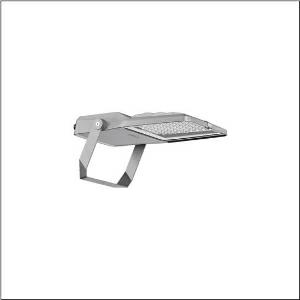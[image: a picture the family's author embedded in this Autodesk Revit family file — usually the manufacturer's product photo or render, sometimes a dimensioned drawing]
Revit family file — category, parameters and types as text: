
# Revit family: floodlight_fl_21_mini___pl33t_5xa7772b2f1a_c476
name_source: partatom
category: Lighting Fixtures
units: mm (PartAtom-declared; Revit-internal decimal feet)

## family parameters
Cut with Voids When Loaded = No
Host = Face
Light Source = No
Part Type = Normal
Room Calculation Point = No
Round Connector Dimension = Use Diameter
Shared = No

## types (1)
- --- (1 x LED, 6170 lm, 45.5 W, 3000K)
    Apparent Load = 46 VA
    CIE Flux Codes = 26 75 99 100 100
    Color Rendering = 70
    Color Temperature = 3000K
    Default Elevation = 1800 mm
    Description = Floodlight FL 21 mini, floodlight, primary light control with lens, of PMMA, primary optical cover: protective disc, of toughened safety glass, transparent, light distribution: PL33T, light emission: direct distribution, installation type: surface-mounted, LED, High Power LED, rated luminous flux: 6.170lm, luminous efficacy: 136lm/W, light colour: 730, colour temperature: 3000K, control gear: ECG iQ, control: Street-Remote, Auto-Match, Temp-Guard, Night-Set, Smart-Wire, Desk-Remote (wireless, voltage-free reading and setting of iQ features in the workshop via application-optimized NFC function/RFID function), optimised constant luminous flux control (CLO 2.0), with terminal, 6-pole, mains connection: 220..240V, AC, 50/60Hz, start of lifetime: 46W, end of lifetime: 48W, reduction: 22W, luminaire housing, of diecast aluminium, powder-coated, Siteco® metallic grey (DB 702S), corrosivity category C5 according to DIN EN ISO 12944, mounting bracket, of steel, galvanised, powder-coated, Siteco® metallic grey (DB 702S), protection rating (complete): IP66, insulation class (complete): insulation class II (safety insulation), certification: CE, ENEC, VDE, protection symbol: D, impact resistance: IK08, permissible operating ambient temperature: -40..+40°C, permissible operating ambient temperature for outdoor applications: -40..+50°C, standard: DIN EN 12944, packaging unit: 1 piece

Light Distribution: PL33T
    Height = 70 mm
    Lamp = 1 x LED
    Lamp Light Flux = 6170 lm
    Lamp Power = 45.5 W
    Lamp count = 1
    Length = 485 mm
    Luminous efficacy = 136 lm/W
    Manufacturer = Siteco
    ModVariant = No
    Model = 5XA7772B2F1A
    Number of Poles = 1
    OnlyDefault = Yes
    Power Factor = 1
    Product Name = Floodlight FL 21 mini | PL33T
    Product group = floodlight | pylon top
    ProductGroupID = 6101
    Protection Class = Protection class II
    Protection Degree = IP 66
    RLX_Detail_Level = 1
    RlxData = <blob elided: 95873 chars, md5=98d4dba4>
    Socket = socket
    Standby Power = 0 W
    System Light Flux = 6170 lm
    System Power = 46 W
    Type Comments = factory setting: luminous flux: 100 % | dim-lin: 254 | 463 mA
    Type Image = l_1006845.jpg
    URL = http://relux.com
    VarID = @adj_060125
    Voltage = 0 V
    Weight = 0.00 kg
    Width = 337 mm

## geometry (parser evidence)
native form markers: Blend x4, Sweep x11
no freeform markers — native parametric forms only
